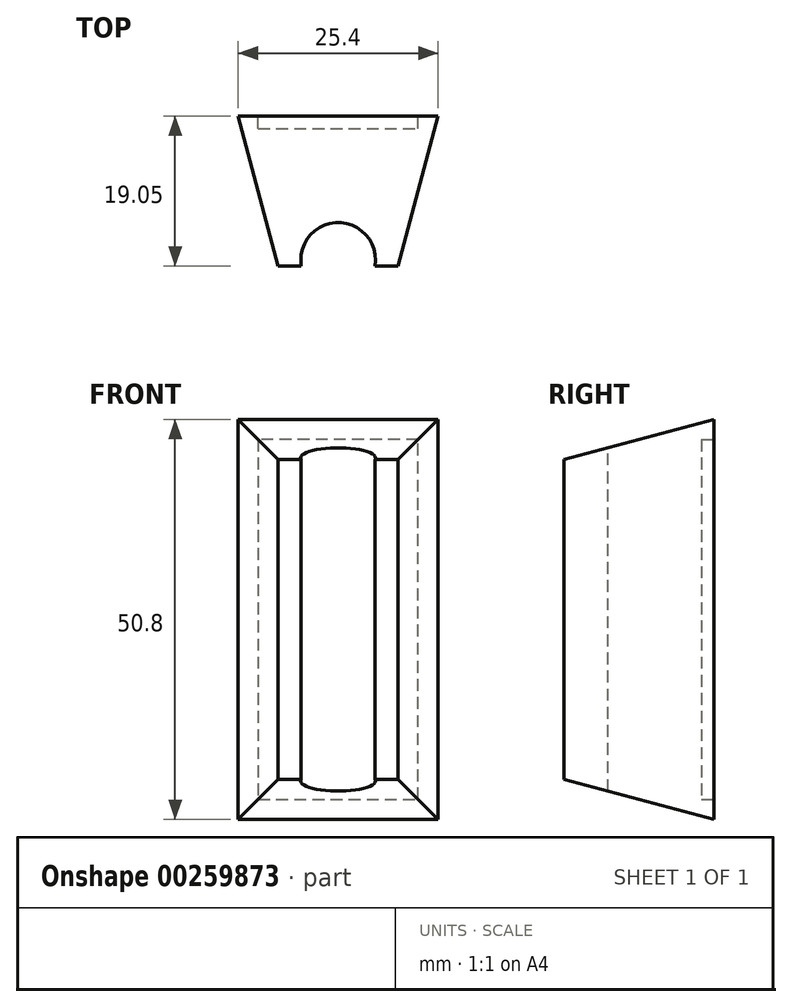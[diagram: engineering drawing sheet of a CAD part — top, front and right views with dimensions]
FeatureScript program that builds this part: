
annotation { "Feature Type Name" : "Feature", "Feature Type Description" : "" }
export const myFeature = defineFeature(function(context is Context, id is Id, definition is map)
    precondition{}
    {
        {
            var Q0;
            Q0=qCreatedBy(makeId("Front.planeOp"),FACE);
            var sketch = newSketch(context, id + "F0", { "sketchPlane" : qUnion([Q0])});
            skLineSegment(sketch, "E0.bottom", {"start": v(-12.7, 25.4) * mm, "end": v(12.7, 25.4) * mm});
            skLineSegment(sketch, "E0.top", {"start": v(-12.7, -25.4) * mm, "end": v(12.7, -25.4) * mm});
            skLineSegment(sketch, "E0.left", {"start": v(-12.7, 25.4) * mm, "end": v(-12.7, -25.4) * mm});
            skLineSegment(sketch, "E0.right", {"start": v(12.7, 25.4) * mm, "end": v(12.7, -25.4) * mm});
            skPoint(sketch, "E0.middle", {"position": v(0, 0) * mm});
            skSolve(sketch);
        }
        {
            var Q0;
            Q0=qCreatedBy(makeId("Front.planeOp"),FACE);
            cPlane(context, id + "F1", {"entities" : qUnion([Q0]), "cplaneType" : CPlaneType.OFFSET, "offset" : 19.05 * mm, "width" : 152.4 * mm, "height" : 152.4 * mm});
        }
        {
            var Q0;
            Q0=qCreatedBy(id+"F1.planeOp",FACE);
            var sketch = newSketch(context, id + "F2", { "sketchPlane" : qUnion([Q0])});
            skLineSegment(sketch, "E1.0", {"start": v(-7.62, 20.32) * mm, "end": v(-7.62, -20.32) * mm});
            skLineSegment(sketch, "E1.1", {"start": v(-7.62, 20.32) * mm, "end": v(7.62, 20.32) * mm});
            skLineSegment(sketch, "E1.2", {"start": v(7.62, 20.32) * mm, "end": v(7.62, -20.32) * mm});
            skLineSegment(sketch, "E1.3", {"start": v(-7.62, -20.32) * mm, "end": v(7.62, -20.32) * mm});
            skSolve(sketch);
        }
        {
            var Q0;
            Q0=makeQuery(id+"F0.imprint","IMPRINT",FACE,{"disambiguationData":[TD([[makeQuery(id+"F0.imprint","IMPRINT",EDGE,{"derivedFrom":sQuery(id+"F0.wireOp",EDGE,"E0.bottom")}),-1.0]])]});
            var Q1;
            Q1=makeQuery(id+"F2.imprint","IMPRINT",FACE,{"disambiguationData":[TD([[makeQuery(id+"F2.imprint","IMPRINT",EDGE,{"derivedFrom":sQuery(id+"F2.wireOp",EDGE,"E1.0")}),1.0]])]});
            loft(context, id + "F3", {"sheetProfilesArray" : [{ "sheetProfileEntities" : qUnion([Q0]) }, { "sheetProfileEntities" : qUnion([Q1]) }]});
        }
        {
            var Q0;
            Q0=makeQuery(id+"F3.opLoft","MID_CAP_EDGE",EDGE,{"disambiguationData":[OSD([sQuery(id+"F0.wireOp",EDGE,"E0.bottom"),sQuery(id+"F0.wireOp",EDGE,"E0.left"),sQuery(id+"F0.wireOp",EDGE,"E0.right")])],"capPos":0.0});
            cPlane(context, id + "F4", {"entities" : qUnion([Q0]), "cplaneType" : CPlaneType.LINE_ANGLE, "offset" : 25.4 * mm, "angle" : 90 * degree, "width" : 152.4 * mm, "height" : 152.4 * mm});
        }
        {
            var Q0;
            Q0=qCreatedBy(id+"F4.planeOp",FACE);
            var sketch = newSketch(context, id + "F5", { "sketchPlane" : qUnion([Q0])});
            skLineSegment(sketch, "E2.0", {"start": v(7.62, -19.05) * mm, "end": v(-7.62, -19.05) * mm, "construction": true});
            skCircle(sketch, "E3", {"center": v(0, -18.26) * mm, "radius": 4.76 * mm});
            skPoint(sketch, "E3.centerSnap0", {"position": v(0, -19.05) * mm});
            skSolve(sketch);
        }
        {
            var Q0;
            Q0=makeQuery(id+"F5.imprint","IMPRINT",FACE,{"disambiguationData":[TD([[makeQuery(id+"F5.imprint","IMPRINT",EDGE,{"derivedFrom":sQuery(id+"F5.wireOp",EDGE,"E3")}),1.0]])]});
            var Q1;
            Q1=sQuery(id+"F5.wireOp",EDGE,"E3");
            extrude(context, id + "F6", {"entities" : qUnion([Q0]), "operationType" : NewBodyOperationType.REMOVE, "surfaceEntities" : qUnion([Q1]), "endBound" : BoundingType.THROUGH_ALL, "oppositeDirection" : true, "depth" : 25.4 * mm});
        }
        {
            var Q0;
            Q0=makeQuery(id+"F3.opLoft","CAP_FACE",FACE,{"disambiguationData":[OSD([makeQuery(id+"F0.imprint","IMPRINT",FACE,{"disambiguationData":[TD([[makeQuery(id+"F0.imprint","IMPRINT",EDGE,{"derivedFrom":sQuery(id+"F0.wireOp",EDGE,"E0.bottom")}),-1.0]])]})])],"isStart":true});
            var sketch = newSketch(context, id + "F7", { "sketchPlane" : qUnion([Q0])});
            skLineSegment(sketch, "E4.0", {"start": v(10.16, -22.86) * mm, "end": v(-10.16, -22.86) * mm});
            skLineSegment(sketch, "E4.1", {"start": v(10.16, 22.86) * mm, "end": v(10.16, -22.86) * mm});
            skLineSegment(sketch, "E4.2", {"start": v(-10.16, 22.86) * mm, "end": v(10.16, 22.86) * mm});
            skLineSegment(sketch, "E4.3", {"start": v(-10.16, -22.86) * mm, "end": v(-10.16, 22.86) * mm});
            skSolve(sketch);
        }
        {
            var Q0;
            Q0=makeQuery(id+"F7.imprint","IMPRINT",FACE,{"disambiguationData":[TD([[makeQuery(id+"F7.imprint","IMPRINT",EDGE,{"derivedFrom":sQuery(id+"F7.wireOp",EDGE,"E4.0")}),-1.0]])]});
            extrude(context, id + "F8", {"entities" : qUnion([Q0]), "operationType" : NewBodyOperationType.REMOVE, "oppositeDirection" : true, "depth" : 1.59 * mm});
        }
    });
